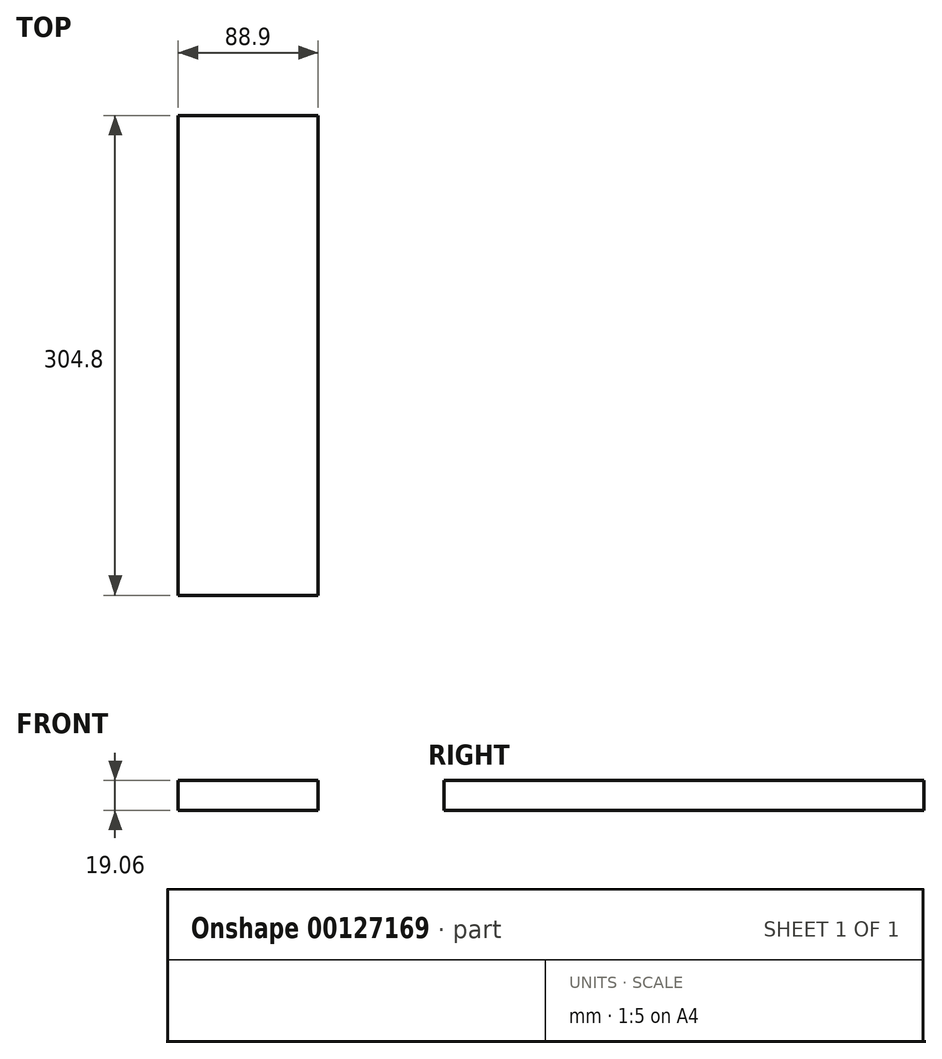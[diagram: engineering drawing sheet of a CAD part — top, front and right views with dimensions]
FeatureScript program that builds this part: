
annotation { "Feature Type Name" : "Feature", "Feature Type Description" : "" }
export const myFeature = defineFeature(function(context is Context, id is Id, definition is map)
    precondition{}
    {
        {
            var Q0;
            Q0=qCreatedBy(makeId("Front.planeOp"),FACE);
            var sketch = newSketch(context, id + "F0", { "sketchPlane" : qUnion([Q0])});
            skLineSegment(sketch, "E0.bottom", {"start": v(44.45, -9.52) * mm, "end": v(-44.45, -9.53) * mm});
            skLineSegment(sketch, "E0.top", {"start": v(44.45, 9.53) * mm, "end": v(-44.45, 9.53) * mm});
            skLineSegment(sketch, "E0.left", {"start": v(44.45, -9.52) * mm, "end": v(44.45, 9.53) * mm});
            skLineSegment(sketch, "E0.right", {"start": v(-44.45, -9.53) * mm, "end": v(-44.45, 9.53) * mm});
            skPoint(sketch, "E0.middle", {"position": v(0, 0) * mm});
            skSolve(sketch);
        }
        {
            var Q0;
            Q0=qSketchRegion(id+"F0",true);
            extrude(context, id + "F1", {"entities" : qUnion([Q0]), "depth" : 304.8 * mm});
        }
    });
